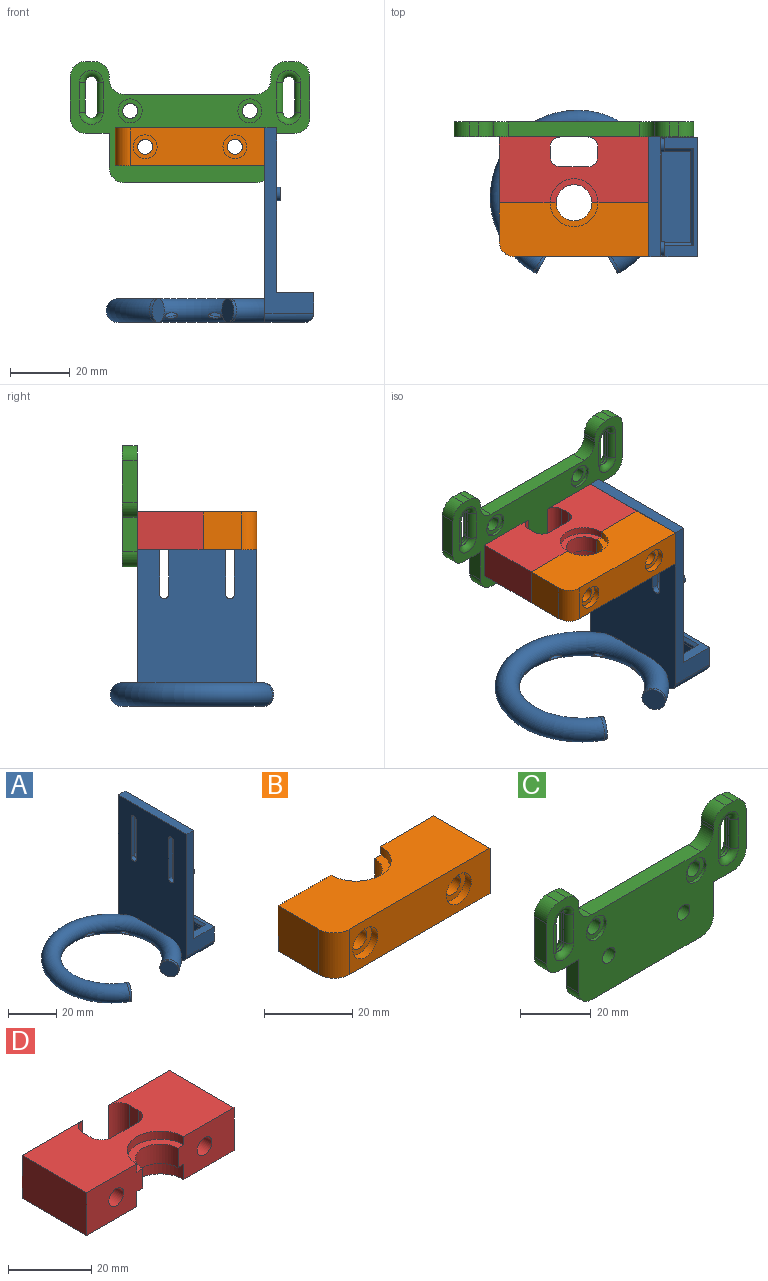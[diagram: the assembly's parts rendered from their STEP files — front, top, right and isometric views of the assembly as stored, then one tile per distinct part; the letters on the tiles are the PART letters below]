
ASSEMBLY  parts=4 mates=2
PART A: 90 faces, bbox 72.2x59.1x65.5 mm
  f0: torus R=25mm, axis (0,0,1), area 2855mm2, adj f1,f3,f5,f6,f64,f65,f66,f69
  f1: cylinder r=4mm len=8mm, axis (0.87,0.5,0), area 25.1mm2, adj f0,f2
  f2: plane 8x6.93mm, normal (-0.87,-0.5,0), area 50.3mm2, adj f1
  f3: cylinder r=4mm len=8mm, axis (-0.87,0.5,0), area 25.1mm2, adj f0,f4
  f4: plane 8x6.93mm, normal (0.87,-0.5,0), area 50.3mm2, adj f3
  f5: plane 14x0.13mm, normal (-1,0,0), area 0.9mm2, adj f0,f40
  f6: plane 65x40mm, normal (-1,0,0), area 2230.1mm2, adj f0,f9,f10,f19,f22,f23,f24,f25
  f7: cylinder r=0.6mm len=4.25mm, axis (-1,0,0), area 16mm2, adj f35,f37
  f8: cylinder r=0.6mm len=4.25mm, axis (-1,0,0), area 16mm2, adj f33,f36
  f9: plane 62x16.3mm, normal (0,-1,0), area 334.1mm2, adj f6,f10,f20,f38,f39,f56
  f10: plane 40x4mm, normal (0,0,1), area 160mm2, adj f6,f9,f19,f20
  f11: plane 20x2mm, normal (0,-1,0), area 40mm2, adj f12,f17,f20,f26
  f12: cylinder r=2.5mm len=5mm, axis (-1,0,0), area 15.7mm2, adj f11,f13,f20,f26
  f13: plane 20x2mm, normal (0,1,0), area 40mm2, adj f12,f17,f20,f26
  f14: plane 20x2mm, normal (0,1,0), area 40mm2, adj f15,f18,f20,f31
  f15: cylinder r=2.5mm len=5mm, axis (-1,0,0), area 15.7mm2, adj f14,f16,f20,f31
  f16: plane 20x2mm, normal (0,-1,0), area 40mm2, adj f15,f18,f20,f31
  f17: cylinder r=2.5mm len=5mm, axis (-1,0,0), area 15.7mm2, adj f11,f13,f20,f26
  f18: cylinder r=2.5mm len=5mm, axis (-1,0,0), area 15.7mm2, adj f14,f16,f20,f31
  f19: plane 62x16.3mm, normal (0,1,0), area 334.1mm2, adj f6,f10,f20,f38,f39,f54
  f20: plane 55x40mm, normal (1,0,0), area 1928.9mm2, adj f9,f10,f11,f12,f13,f14,f15,f16
  f21: plane 27.26x5.2mm, normal (-1,0,0), area 49.8mm2, adj f57,f58,f63,f67,f68
  f22: cylinder r=1.5mm len=3mm, axis (-1,0,0), area 9.4mm2, adj f6,f23,f25,f26
  f23: plane 20x2mm, normal (0,1,0), area 40mm2, adj f6,f22,f24,f26
  f24: cylinder r=1.5mm len=3mm, axis (-1,0,0), area 9.4mm2, adj f6,f23,f25,f26
  f25: plane 20x2mm, normal (0,-1,0), area 40mm2, adj f6,f22,f24,f26
  f26: plane 25x5mm, normal (1,0,0), area 52.6mm2, adj f11,f12,f13,f17,f22,f23,f24,f25
  f27: plane 20x2mm, normal (0,1,0), area 40mm2, adj f6,f28,f30,f31
  f28: cylinder r=1.5mm len=3mm, axis (-1,0,0), area 9.4mm2, adj f6,f27,f29,f31
  f29: plane 20x2mm, normal (0,-1,0), area 40mm2, adj f6,f28,f30,f31
  f30: cylinder r=1.5mm len=3mm, axis (-1,0,0), area 9.4mm2, adj f6,f27,f29,f31
  f31: plane 25x5mm, normal (1,0,0), area 52.6mm2, adj f14,f15,f16,f18,f27,f28,f29,f30
  f32: cylinder r=2.25mm len=4.5mm, axis (-1,0,0), area 17.7mm2, adj f20,f33
  f33: plane 4.5x4.5mm, normal (1,0,0), area 14.8mm2, adj f8,f32
  f34: cylinder r=2.25mm len=4.5mm, axis (-1,0,0), area 17.7mm2, adj f20,f35
  f35: plane 4.5x4.5mm, normal (1,0,0), area 14.8mm2, adj f7,f34
  f36: plane 1.2x1.2mm, normal (1,0,0), area 1.1mm2, adj f8
  f37: plane 1.2x1.2mm, normal (1,0,0), area 1.1mm2, adj f7
  f38: plane 40x12.3mm, normal (0,0,1), area 143.2mm2, adj f9,f19,f20,f39,f42,f51,f52,f53
  f39: plane 40x7mm, normal (1,0,0), area 280mm2, adj f9,f19,f38,f55
  f40: plane 34x13.3mm, normal (0,0,-1), area 452.2mm2, adj f5,f6,f54,f55,f56
  f41: plane 9.7x1mm, normal (0,1,0), area 9.7mm2, adj f42,f44,f45,f53
  f42: plane 32.6x2mm, normal (1,0,0), area 62.2mm2, adj f38,f41,f43,f45,f51,f53
  f43: plane 9.7x1mm, normal (0,-1,0), area 9.7mm2, adj f42,f44,f45,f51
  f44: plane 30.6x1mm, normal (-1,0,0), area 30.6mm2, adj f41,f43,f45,f52
  f45: plane 36x12.3mm, normal (0,0,-1), area 146mm2, adj f41,f42,f43,f44,f47,f48,f49,f50
  f46: plane 36x12.3mm, normal (0,0,1), area 442.8mm2, adj f47,f48,f49,f50
  f47: plane 12.3x6mm, normal (0,1,0), area 73.8mm2, adj f45,f46,f48,f50
  f48: plane 36x6mm, normal (-1,0,0), area 216mm2, adj f45,f46,f47,f49
  f49: plane 12.3x6mm, normal (0,-1,0), area 73.8mm2, adj f45,f46,f48,f50
  f50: plane 36.55x6.55mm, normal (1,0,0), area 138.1mm2, adj f45,f46,f47,f49,f57,f58,f67,f68
  f51: plane 10.7x1mm, normal (0,-0.71,0.71), area 14.4mm2, adj f38,f42,f43,f52
  f52: plane 32.6x1mm, normal (-0.71,0,0.71), area 44.7mm2, adj f38,f44,f51,f53
  f53: plane 10.7x1mm, normal (0,0.71,0.71), area 14.4mm2, adj f38,f41,f42,f52
  f54: cylinder r=3mm len=16.3mm, axis (-1,0,0), area 69.7mm2, adj f6,f19,f40,f55
  f55: cylinder r=3mm len=40mm, axis (0,1,0), area 174.4mm2, adj f39,f40,f54,f56
  f56: cylinder r=3mm len=16.3mm, axis (1,0,0), area 69.7mm2, adj f6,f9,f40,f55
  f57: extruded ~15.49x4.34mm, area 67.4mm2, adj f21,f50,f61
  f58: extruded ~7.45x4.2mm, area 35.2mm2, adj f21,f50,f62,f67,f68
  f59: plane 5.2x4.5mm, normal (0.87,0.5,0), area 21.2mm2, adj f63
  f60: plane 5.2x4.5mm, normal (-0.87,0.5,0), area 21.2mm2, adj f63
  f61: plane 12.94x2.52mm, normal (1,0,0), area 4mm2, adj f57,f63
  f62: plane 2.38x0.21mm, normal (1,0,0), area 0.1mm2, adj f58,f63
  f63: torus R=25mm, axis (0,0,1), area 1853mm2, adj f21,f59,f60,f61,f62,f64,f65,f66
  f64: plane 3.5x3.15mm, normal (0,0,-1), area 4.8mm2, adj f0,f63,f65
  f65: bspline ~6.65x6.29mm, area 9.4mm2, adj f0,f63,f64
  f66: bspline ~8.36x4.7mm, area 13.2mm2, adj f0,f63
  f67: plane 2.01x1.95mm, normal (0,0,-1), area 3.7mm2, adj f21,f50,f58,f68
  f68: bspline ~5.44x3.95mm, area 7mm2, adj f21,f50,f58,f67
  f69: bspline ~7.8x6.2mm, area 13.2mm2, adj f0,f63
  f70: bspline ~1.77x0.64mm, area 0mm2, adj f63,f71
  f71: plane 1.77x0.64mm, normal (0,0,-1), area 0.2mm2, adj f63,f70
  f72: plane 1.59x0.58mm, normal (0,0,-1), area 0.2mm2, adj f63,f73
  f73: bspline ~9.6x6.49mm, area 16mm2, adj f0,f63,f72
  f74: bspline ~1.77x0.64mm, area 0mm2, adj f63,f75
  f75: plane 1.77x0.64mm, normal (0,0,-1), area 0.2mm2, adj f63,f74
  f76: plane 1.59x0.58mm, normal (0,0,-1), area 0.2mm2, adj f63,f77
  f77: bspline ~9.57x6.56mm, area 15.9mm2, adj f0,f63,f76
  f78: bspline ~10.3x8.32mm, area 18.1mm2, adj f0,f63,f79
  f79: plane 3.2x1.86mm, normal (0,0,-1), area 1.6mm2, adj f63,f78
  f80: plane 3.55x2.1mm, normal (0,0,-1), area 1.8mm2, adj f63,f81
  f81: bspline ~3.8x2.63mm, area 2mm2, adj f63,f80
  f82: bspline ~10.94x6.59mm, area 18.1mm2, adj f0,f63,f83
  f83: plane 3.64x0.94mm, normal (0,0,-1), area 1.6mm2, adj f63,f82
  f84: plane 4.04x1.13mm, normal (0,0,-1), area 1.8mm2, adj f63,f85
  f85: bspline ~4.1x1.74mm, area 2mm2, adj f63,f84
  f86: bspline ~4.29x3.78mm, area 3.4mm2, adj f63,f87
  f87: plane 3.77x3.19mm, normal (0,0,-1), area 3.1mm2, adj f63,f86
  f88: plane 3.4x2.85mm, normal (0,0,-1), area 2.7mm2, adj f63,f89
  f89: bspline ~10.26x9.6mm, area 18.6mm2, adj f0,f63,f88
PART B: 19 faces, bbox 50x18x12.6 mm
  f0: cylinder r=2.5mm len=16mm, axis (0,-1,0), area 251.3mm2, adj f13,f18
  f1: plane 45x12.6mm, normal (0,-1,0), area 466.5mm2, adj f6,f8,f9,f14,f15,f17
  f2: cylinder r=2.5mm len=16mm, axis (0,-1,0), area 251.3mm2, adj f12,f16
  f3: plane 16x8mm, normal (0,0,-1), area 44mm2, adj f5,f11,f12,f13
  f4: plane 16x8mm, normal (0,0,1), area 44mm2, adj f5,f7,f12,f13
  f5: cylinder r=6mm len=12mm, axis (0,0,-1), area 107.4mm2, adj f3,f4,f12,f13
  f6: plane 50x18mm, normal (0,0,1), area 794.1mm2, adj f1,f7,f9,f10,f12,f13,f14
  f7: cylinder r=8mm len=16mm, axis (0,0,-1), area 60.3mm2, adj f4,f6,f12,f13
  f8: plane 50x18mm, normal (0,0,-1), area 794.1mm2, adj f1,f9,f10,f11,f12,f13,f14
  f9: plane 18x12.6mm, normal (1,0,0), area 226.8mm2, adj f1,f6,f8,f13
  f10: plane 13x12.6mm, normal (-1,0,0), area 163.8mm2, adj f6,f8,f12,f14
  f11: cylinder r=8mm len=16mm, axis (0,0,-1), area 113.1mm2, adj f3,f8,f12,f13
  f12: plane 19x12.6mm, normal (0,1,0), area 206mm2, adj f2,f3,f4,f5,f6,f7,f8,f10
  f13: plane 19x12.6mm, normal (0,1,0), area 206mm2, adj f0,f3,f4,f5,f6,f7,f8,f9
  f14: cylinder r=5mm len=12.6mm, axis (0,0,1), area 99mm2, adj f1,f6,f8,f10
  f15: cylinder r=4mm len=8mm, axis (0,-1,0), area 50.3mm2, adj f1,f16
  f16: plane 8x8mm, normal (0,-1,0), area 30.6mm2, adj f2,f15
  f17: cylinder r=4mm len=8mm, axis (0,-1,0), area 50.3mm2, adj f1,f18
  f18: plane 8x8mm, normal (0,-1,0), area 30.6mm2, adj f0,f17
PART C: 70 faces, bbox 80x5x40.5 mm
  f0: plane 80x40.5mm, normal (0,1,0), area 1759.9mm2, adj f5,f6,f7,f8,f9,f10,f11,f12
  f1: plane 10x1mm, normal (1,0,0), area 10mm2, adj f44,f48,f49,f51
  f2: plane 10x1mm, normal (-1,0,0), area 10mm2, adj f42,f46,f48,f49
  f3: plane 10x1mm, normal (1,0,0), area 10mm2, adj f32,f34,f37,f40
  f4: plane 10x1mm, normal (-1,0,0), area 10mm2, adj f36,f37,f40,f41
  f5: plane 5x1mm, normal (1,0,0), area 5mm2, adj f0,f21,f22,f25
  f6: plane 5x3mm, normal (0,0,1), area 15mm2, adj f0,f21,f22,f23
  f7: plane 14x5mm, normal (-1,0,0), area 70mm2, adj f0,f21,f23,f24
  f8: plane 8x5mm, normal (0,0,-1), area 40mm2, adj f0,f9,f21,f24
  f9: plane 11.5x5mm, normal (-1,0,0), area 57.5mm2, adj f0,f8,f21,f27
  f10: plane 44x5mm, normal (0,0,-1), area 220mm2, adj f0,f21,f27,f28
  f11: plane 11.5x5mm, normal (1,0,0), area 57.5mm2, adj f0,f12,f21,f28
  f12: plane 8x5mm, normal (0,0,-1), area 40mm2, adj f0,f11,f21,f29
  f13: plane 14x5mm, normal (1,0,0), area 70mm2, adj f0,f21,f29,f30
  f14: plane 5x3mm, normal (0,0,1), area 15mm2, adj f0,f21,f30,f31
  f15: plane 5x1mm, normal (-1,0,0), area 5mm2, adj f0,f21,f26,f31
  f16: cylinder r=2.5mm len=5mm, axis (0,1,0), area 55mm2, adj f21,f58
  f17: cylinder r=4mm len=8mm, axis (0,1,0), area 25.1mm2, adj f21,f69
  f18: cylinder r=4mm len=8mm, axis (0,1,0), area 25.1mm2, adj f21,f67
  f19: plane 44x5mm, normal (0,0,1), area 220mm2, adj f0,f21,f25,f26
  f20: cylinder r=2.5mm len=5mm, axis (0,1,0), area 55mm2, adj f21,f65
  f21: plane 80x40.5mm, normal (0,-1,0), area 1784.5mm2, adj f5,f6,f7,f8,f9,f10,f11,f12
  f22: cylinder r=5mm len=5mm, axis (0,-1,0), area 39.3mm2, adj f0,f5,f6,f21
  f23: cylinder r=5mm len=5mm, axis (0,1,0), area 39.3mm2, adj f0,f6,f7,f21
  f24: cylinder r=5mm len=5mm, axis (0,-1,0), area 39.3mm2, adj f0,f7,f8,f21
  f25: cylinder r=5mm len=5mm, axis (0,1,0), area 39.3mm2, adj f0,f5,f19,f21
  f26: cylinder r=5mm len=5mm, axis (0,-1,0), area 39.3mm2, adj f0,f15,f19,f21
  f27: cylinder r=5mm len=5mm, axis (0,-1,0), area 39.3mm2, adj f0,f9,f10,f21
  f28: cylinder r=5mm len=5mm, axis (0,1,0), area 39.3mm2, adj f0,f10,f11,f21
  f29: cylinder r=5mm len=5mm, axis (0,-1,0), area 39.3mm2, adj f0,f12,f13,f21
  f30: cylinder r=5mm len=5mm, axis (0,1,0), area 39.3mm2, adj f0,f13,f14,f21
  f31: cylinder r=5mm len=5mm, axis (0,-1,0), area 39.3mm2, adj f0,f14,f15,f21
  f32: cylinder r=2mm len=10mm, axis (0,0,1), area 31.4mm2, adj f0,f3,f33,f35
  f33: torus R=4mm, axis (0,-1,0), area 26.9mm2, adj f0,f32,f36,f37
  f34: cylinder r=2mm len=10mm, axis (0,0,-1), area 31.4mm2, adj f3,f21,f38,f39
  f35: torus R=4mm, axis (0,-1,0), area 26.9mm2, adj f0,f32,f36,f40
  f36: cylinder r=2mm len=10mm, axis (0,0,-1), area 31.4mm2, adj f0,f4,f33,f35
  f37: cylinder r=2mm len=4mm, axis (0,-1,0), area 6.3mm2, adj f3,f4,f33,f38
  f38: torus R=4mm, axis (0,-1,0), area 26.9mm2, adj f21,f34,f37,f41
  f39: torus R=4mm, axis (0,-1,0), area 26.9mm2, adj f21,f34,f40,f41
  f40: cylinder r=2mm len=4mm, axis (0,1,0), area 6.3mm2, adj f3,f4,f35,f39
  f41: cylinder r=2mm len=10mm, axis (0,0,1), area 31.4mm2, adj f4,f21,f38,f39
  f42: cylinder r=2mm len=10mm, axis (0,0,-1), area 31.4mm2, adj f0,f2,f43,f45
  f43: torus R=4mm, axis (0,-1,0), area 26.9mm2, adj f0,f42,f44,f48
  f44: cylinder r=2mm len=10mm, axis (0,0,1), area 31.4mm2, adj f0,f1,f43,f45
  f45: torus R=4mm, axis (0,-1,0), area 26.9mm2, adj f0,f42,f44,f49
  f46: cylinder r=2mm len=10mm, axis (0,0,1), area 31.4mm2, adj f2,f21,f47,f50
  f47: torus R=4mm, axis (0,-1,0), area 26.9mm2, adj f21,f46,f48,f51
  f48: cylinder r=2mm len=4mm, axis (0,-1,0), area 6.3mm2, adj f1,f2,f43,f47
  f49: cylinder r=2mm len=4mm, axis (0,1,0), area 6.3mm2, adj f1,f2,f45,f50
  f50: torus R=4mm, axis (0,-1,0), area 26.9mm2, adj f21,f46,f49,f51
  f51: cylinder r=2mm len=10mm, axis (0,0,-1), area 31.4mm2, adj f1,f21,f47,f50
  f52: plane 4.63x1.62mm, normal (-0.33,0,-0.94), area 7.4mm2, adj f0,f53,f57,f58
  f53: plane 3.72x3.21mm, normal (0.65,0,-0.76), area 7.4mm2, adj f0,f52,f54,f58
  f54: plane 4.82x1.5mm, normal (0.98,0,0.19), area 7.4mm2, adj f0,f53,f55,f58
  f55: plane 4.63x1.62mm, normal (0.33,0,0.94), area 7.4mm2, adj f0,f54,f56,f58
  f56: plane 3.72x3.21mm, normal (-0.65,0,0.76), area 7.4mm2, adj f0,f55,f57,f58
  f57: plane 4.82x1.5mm, normal (-0.98,0,-0.19), area 7.4mm2, adj f0,f52,f56,f58
  f58: plane 9.64x9.27mm, normal (0,1,0), area 42.9mm2, adj f16,f52,f53,f54,f55,f56,f57
  f59: plane 4.63x1.62mm, normal (-0.33,0,0.94), area 7.4mm2, adj f0,f60,f64,f65
  f60: plane 4.82x1.5mm, normal (-0.98,0,0.19), area 7.4mm2, adj f0,f59,f61,f65
  f61: plane 3.72x3.21mm, normal (-0.65,0,-0.76), area 7.4mm2, adj f0,f60,f62,f65
  f62: plane 4.63x1.62mm, normal (0.33,0,-0.94), area 7.4mm2, adj f0,f61,f63,f65
  f63: plane 4.82x1.5mm, normal (0.98,0,-0.19), area 7.4mm2, adj f0,f62,f64,f65
  f64: plane 3.72x3.21mm, normal (0.65,0,0.76), area 7.4mm2, adj f0,f59,f63,f65
  f65: plane 9.64x9.27mm, normal (0,1,0), area 42.9mm2, adj f20,f59,f60,f61,f62,f63,f64
  f66: cylinder r=2.5mm len=5mm, axis (0,1,0), area 62.8mm2, adj f0,f67
  f67: plane 8x8mm, normal (0,-1,0), area 30.6mm2, adj f18,f66
  f68: cylinder r=2.5mm len=5mm, axis (0,1,0), area 62.8mm2, adj f0,f69
  f69: plane 8x8mm, normal (0,-1,0), area 30.6mm2, adj f17,f68
PART D: 22 faces, bbox 50x22x12.6 mm
  f0: cylinder r=8mm len=16mm, axis (0,0,-1), area 113.1mm2, adj f5,f8,f20,f21
  f1: plane 22x12.6mm, normal (-1,0,0), area 277.2mm2, adj f4,f5,f19,f20
  f2: plane 22x12.6mm, normal (1,0,0), area 277.2mm2, adj f4,f5,f11,f21
  f3: cylinder r=8mm len=16mm, axis (0,0,-1), area 60.3mm2, adj f4,f7,f20,f21
  f4: plane 50x22mm, normal (0,0,1), area 850mm2, adj f1,f2,f3,f11,f12,f13,f14,f15
  f5: plane 50x22mm, normal (0,0,-1), area 850mm2, adj f0,f1,f2,f11,f12,f13,f14,f15
  f6: cylinder r=6mm len=12mm, axis (0,0,-1), area 107.4mm2, adj f7,f8,f20,f21
  f7: plane 16x8mm, normal (0,0,1), area 44mm2, adj f3,f6,f20,f21
  f8: plane 16x8mm, normal (0,0,-1), area 44mm2, adj f0,f6,f20,f21
  f9: cylinder r=2.5mm len=22mm, axis (0,-1,0), area 345.6mm2, adj f11,f21
  f10: cylinder r=2.5mm len=22mm, axis (0,-1,0), area 345.6mm2, adj f19,f20
  f11: plane 20.5x12.6mm, normal (0,1,0), area 238.7mm2, adj f2,f4,f5,f9,f12
  f12: cylinder r=3.5mm len=12.6mm, axis (0,0,-1), area 69.3mm2, adj f4,f5,f11,f13
  f13: plane 12.6x3mm, normal (-1,0,0), area 37.8mm2, adj f4,f5,f12,f14
  f14: cylinder r=3.5mm len=12.6mm, axis (0,0,-1), area 69.3mm2, adj f4,f5,f13,f15
  f15: plane 12.6x9mm, normal (0,1,0), area 113.4mm2, adj f4,f5,f14,f16
  f16: cylinder r=3.5mm len=12.6mm, axis (0,0,-1), area 69.3mm2, adj f4,f5,f15,f17
  f17: plane 12.6x3mm, normal (1,0,0), area 37.8mm2, adj f4,f5,f16,f18
  f18: cylinder r=3.5mm len=12.6mm, axis (0,0,-1), area 69.3mm2, adj f4,f5,f17,f19
  f19: plane 20.5x12.6mm, normal (0,1,0), area 238.7mm2, adj f1,f4,f5,f10,f18
  f20: plane 19x12.6mm, normal (0,-1,0), area 206mm2, adj f0,f1,f3,f4,f5,f6,f7,f8
  f21: plane 19x12.6mm, normal (0,-1,0), area 206mm2, adj f0,f2,f3,f4,f5,f6,f7,f8
PLACE A t=(12.7,-56.57,-77.64)mm
PLACE B t=(11.7,-58.57,-29.24)mm
PLACE C t=(11.7,-31.57,-20.19)mm
PLACE D t=(11.7,-58.57,-29.24)mm
MATE planar C.f20 <-> D.f10  axis (0,-1,0) through (-3.3,-36.57,-22.94)mm
MATE planar A.f6 <-> B.f9  axis (-1,0,0) through (36.7,-76.57,-16.64)mm
